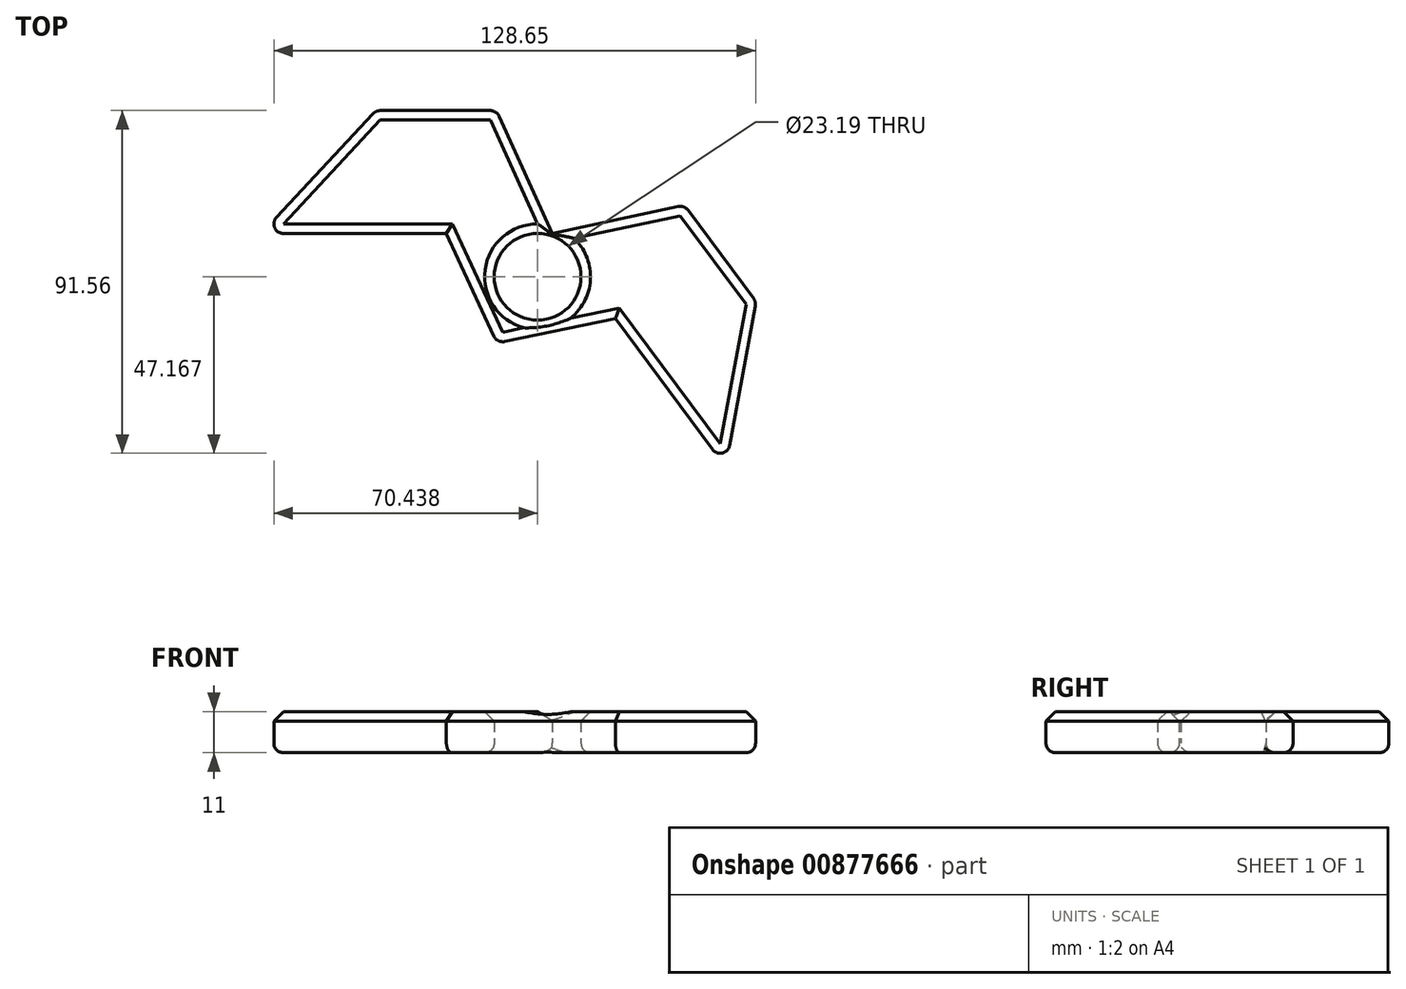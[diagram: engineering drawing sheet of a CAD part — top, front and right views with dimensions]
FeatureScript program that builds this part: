
annotation { "Feature Type Name" : "Feature", "Feature Type Description" : "" }
export const myFeature = defineFeature(function(context is Context, id is Id, definition is map)
    precondition{}
    {
        {
            var Q0;
            Q0=qCreatedBy(makeId("Top.planeOp"),FACE);
            var sketch = newSketch(context, id + "F0", { "sketchPlane" : qUnion([Q0])});
            skLineSegment(sketch, "E0", {"start": v(-47.12, 48.27) * mm, "end": v(-14.94, 48.27) * mm});
            skLineSegment(sketch, "E1", {"start": v(-47.12, 48.27) * mm, "end": v(-47.12, 15.46) * mm});
            skLineSegment(sketch, "E2", {"start": v(-14.94, 48.27) * mm, "end": v(0, 15.46) * mm});
            skLineSegment(sketch, "E3", {"start": v(-47.12, 15.46) * mm, "end": v(0, 15.46) * mm});
            skLineSegment(sketch, "E4", {"start": v(-47.12, 48.27) * mm, "end": v(-77.68, 15.46) * mm});
            skLineSegment(sketch, "E5", {"start": v(-77.68, 15.46) * mm, "end": v(-47.12, 15.46) * mm});
            skLineSegment(sketch, "E6", {"start": v(0, 15.46) * mm, "end": v(-14.75, -13.83) * mm});
            skLineSegment(sketch, "E7", {"start": v(-28.3, 15.46) * mm, "end": v(-14.75, -13.83) * mm});
            skLineSegment(sketch, "E8", {"start": v(-77.68, 15.46) * mm, "end": v(-5.65, 27.87) * mm});
            skLineSegment(sketch, "E9", {"start": v(-28.3, 15.46) * mm, "end": v(-30.86, 21) * mm});
            skLineSegment(sketch, "E10", {"start": v(-30.88, 21) * mm, "end": v(-33.17, 23.13) * mm});
            skSolve(sketch);
        }
        {
            var Q0;
            Q0 = qSketchRegion(id + "F0", true);
            extrude(context, id + "F1", {"entities" : qUnion([Q0]), "depth" : 11 * mm, "offsetDistance" : 25.4 * mm});
        }
        {
            var Q0;
            Q0=makeQuery(id+"F1.opExtrude","SWEPT_BODY",BODY,{"disambiguationData":[OSD([sQuery(id+"F0.wireOp",EDGE,"E0"),sQuery(id+"F0.wireOp",EDGE,"E2"),sQuery(id+"F0.wireOp",EDGE,"E3"),sQuery(id+"F0.wireOp",EDGE,"E4"),sQuery(id+"F0.wireOp",EDGE,"E5"),sQuery(id+"F0.wireOp",EDGE,"E6"),sQuery(id+"F0.wireOp",EDGE,"E7")])]});
            var Q1;
            Q1=makeQuery(id+"F1.opExtrude","SWEPT_FACE",FACE,{"disambiguationData":[OSD([sQuery(id+"F0.wireOp",EDGE,"E6")])]});
            mirror(context, id + "F2", {"operationType" : NewBodyOperationType.ADD, "entities" : qUnion([Q0]), "mirrorPlane" : qUnion([Q1])});
        }
        {
            var Q0;
            Q0=qCreatedBy(makeId("Top.planeOp"),FACE);
            var sketch = newSketch(context, id + "F3", { "sketchPlane" : qUnion([Q0])});
            skCircle(sketch, "E11", {"center": v(-3.95, 3.88) * mm, "radius": 11.6 * mm});
            skCircle(sketch, "E12", {"center": v(-3.95, 3.88) * mm, "radius": 12.12 * mm});
            skCircle(sketch, "E13", {"center": v(-37.67, -10.83) * mm, "radius": 19.1 * mm});
            skSolve(sketch);
        }
        {
            var Q0;
            Q0=makeQuery(id+"F3.imprint","IMPRINT",FACE,{"disambiguationData":[TD([[makeQuery(id+"F3.imprint","IMPRINT",EDGE,{"derivedFrom":sQuery(id+"F3.wireOp",EDGE,"E11")}),1.0]])]});
            extrude(context, id + "F4", {"entities" : qUnion([Q0]), "operationType" : NewBodyOperationType.REMOVE, "depth" : 21.84 * mm, "offsetDistance" : 25.4 * mm});
        }
        {
            var Q0;
            Q0=makeQuery(id+"F2.opPattern","COPY",EDGE,{"derivedFrom":makeQuery(id+"F1.opExtrude","SWEPT_EDGE",EDGE,{"disambiguationData":[OSD([sQuery(id+"F0.wireOp",EDGE,"E4"),sQuery(id+"F0.wireOp",EDGE,"E5"),sQuery(id+"F0.wireOp",EDGE,"E8")])]}),"instanceName":"1"});
            var Q1;
            Q1=makeQuery(id+"F2.opPattern","COPY",EDGE,{"derivedFrom":makeQuery(id+"F1.opExtrude","SWEPT_EDGE",EDGE,{"disambiguationData":[OSD([sQuery(id+"F0.wireOp",EDGE,"E0"),sQuery(id+"F0.wireOp",EDGE,"E1"),sQuery(id+"F0.wireOp",EDGE,"E4")])]}),"instanceName":"1"});
            var Q2;
            Q2=makeQuery(id+"F2.opPattern","COPY",EDGE,{"derivedFrom":makeQuery(id+"F1.opExtrude","SWEPT_EDGE",EDGE,{"disambiguationData":[OSD([sQuery(id+"F0.wireOp",EDGE,"E0"),sQuery(id+"F0.wireOp",EDGE,"E2")])]}),"instanceName":"1"});
            var Q3;
            Q3=makeQuery(id+"F1.opExtrude","SWEPT_EDGE",EDGE,{"disambiguationData":[OSD([sQuery(id+"F0.wireOp",EDGE,"E0"),sQuery(id+"F0.wireOp",EDGE,"E2")])]});
            var Q4;
            Q4=makeQuery(id+"F1.opExtrude","SWEPT_EDGE",EDGE,{"disambiguationData":[OSD([sQuery(id+"F0.wireOp",EDGE,"E0"),sQuery(id+"F0.wireOp",EDGE,"E1"),sQuery(id+"F0.wireOp",EDGE,"E4")])]});
            var Q5;
            Q5=makeQuery(id+"F1.opExtrude","SWEPT_EDGE",EDGE,{"disambiguationData":[OSD([sQuery(id+"F0.wireOp",EDGE,"E4"),sQuery(id+"F0.wireOp",EDGE,"E5"),sQuery(id+"F0.wireOp",EDGE,"E8")])]});
            var Q6;
            {var subQ0=makeQuery(id+"F1.opExtrude","SWEPT_EDGE",EDGE,{"disambiguationData":[OSD([sQuery(id+"F0.wireOp",EDGE,"E6"),sQuery(id+"F0.wireOp",EDGE,"E7")])]});Q6=makeQuery(id+"F2.boolean.opBoolean","MERGE",EDGE,{"derivedFrom":[subQ0,makeQuery(id+"F2.opPattern","COPY",EDGE,{"derivedFrom":subQ0,"instanceName":"1"})]});}
            var Q7;
            {var subQ0=makeQuery(id+"F1.opExtrude","CAP_FACE",FACE,{"disambiguationData":[OSD([sQuery(id+"F0.wireOp",EDGE,"E0"),sQuery(id+"F0.wireOp",EDGE,"E2"),sQuery(id+"F0.wireOp",EDGE,"E3"),sQuery(id+"F0.wireOp",EDGE,"E4"),sQuery(id+"F0.wireOp",EDGE,"E5"),sQuery(id+"F0.wireOp",EDGE,"E6"),sQuery(id+"F0.wireOp",EDGE,"E7")])],"isStart":true});Q7=makeQuery(id+"F2.boolean.opBoolean","MERGE",FACE,{"derivedFrom":[subQ0,makeQuery(id+"F2.opPattern","COPY",FACE,{"derivedFrom":subQ0,"instanceName":"1"})]});}
            fillet(context, id + "F5", {"entities" : qUnion([Q0, Q1, Q2, Q3, Q4, Q5, Q6, Q7]), "radius" : 2.54 * mm, "tangentPropagation" : true, "allowEdgeOverflow" : false});
        }
        {
            var Q0;
            {var subQ0=makeQuery(id+"F1.opExtrude","CAP_FACE",FACE,{"disambiguationData":[OSD([sQuery(id+"F0.wireOp",EDGE,"E0"),sQuery(id+"F0.wireOp",EDGE,"E2"),sQuery(id+"F0.wireOp",EDGE,"E3"),sQuery(id+"F0.wireOp",EDGE,"E4"),sQuery(id+"F0.wireOp",EDGE,"E5"),sQuery(id+"F0.wireOp",EDGE,"E6"),sQuery(id+"F0.wireOp",EDGE,"E7")])],"isStart":false});Q0=makeQuery(id+"F2.boolean.opBoolean","MERGE",FACE,{"derivedFrom":[subQ0,makeQuery(id+"F2.opPattern","COPY",FACE,{"derivedFrom":subQ0,"instanceName":"1"})]});}
            chamfer(context, id + "F6", {"entities" : qUnion([Q0]), "width" : 2.54 * mm, "tangentPropagation" : true});
        }
    });
